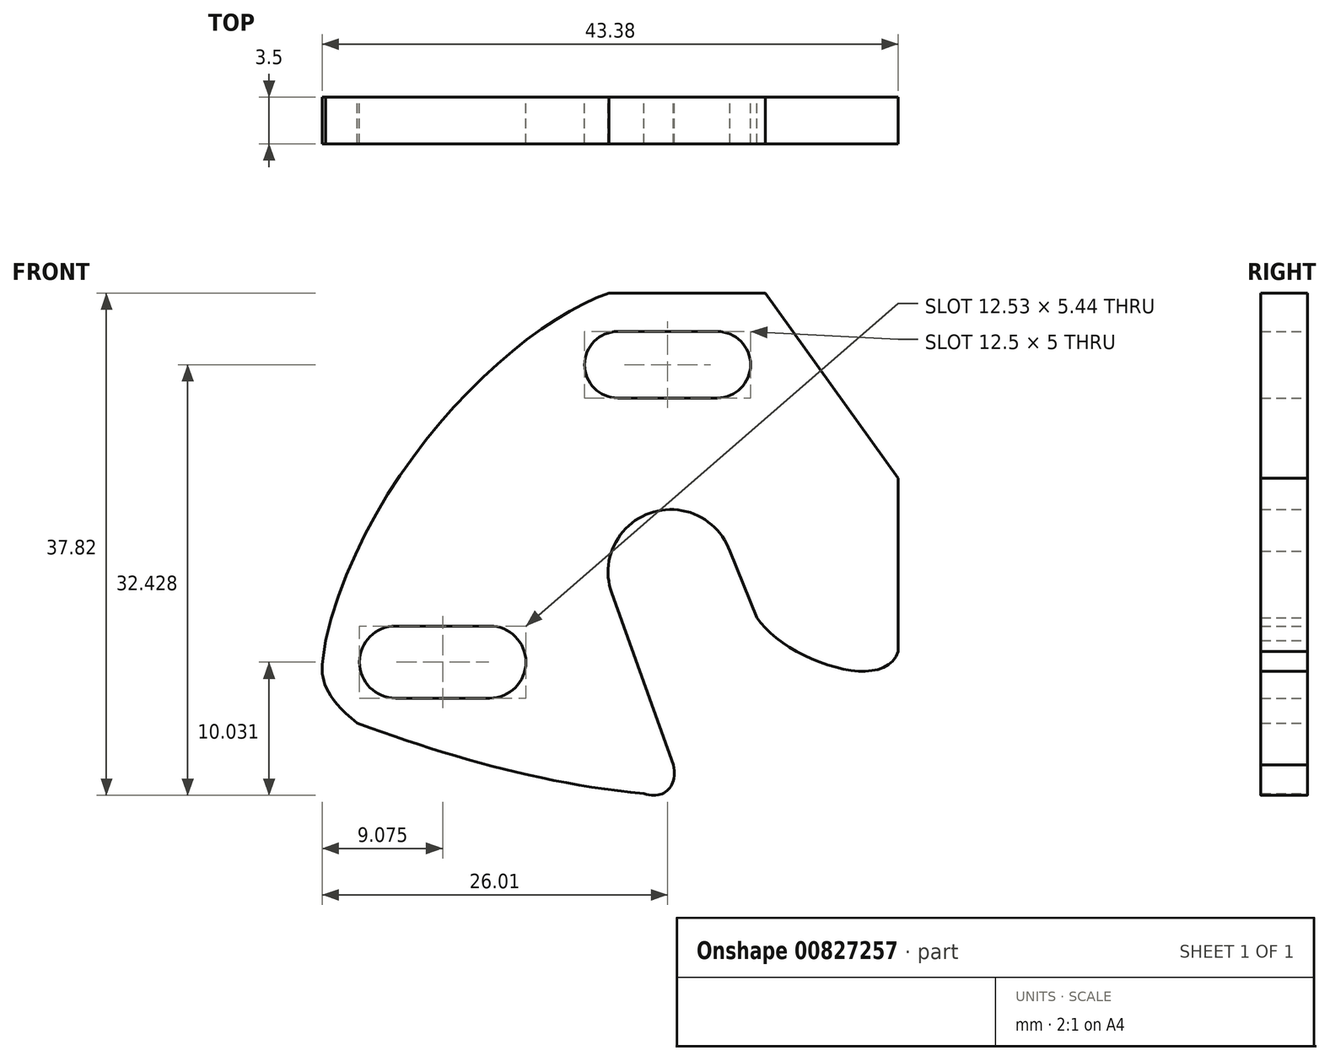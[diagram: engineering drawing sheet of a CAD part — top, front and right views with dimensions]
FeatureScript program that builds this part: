
annotation { "Feature Type Name" : "Feature", "Feature Type Description" : "" }
export const myFeature = defineFeature(function(context is Context, id is Id, definition is map)
    precondition{}
    {
        {
            var Q0;
            Q0=qCreatedBy(makeId("Front.planeOp"),FACE);
            var sketch = newSketch(context, id + "F0", { "sketchPlane" : qUnion([Q0])});
            skLineSegment(sketch, "E0", {"start": v(-0.66, 19.43) * mm, "end": v(11.11, 19.43) * mm});
            skLineSegment(sketch, "E1", {"start": v(11.11, 19.43) * mm, "end": v(21.12, 5.5) * mm});
            skLineSegment(sketch, "E2", {"start": v(21.12, 5.5) * mm, "end": v(21.12, -7.55) * mm});
            skLineSegment(sketch, "E3", {"start": v(0, 16.54) * mm, "end": v(7.5, 16.54) * mm});
            skLineSegment(sketch, "E4", {"start": v(0, 11.54) * mm, "end": v(7.5, 11.54) * mm});
            skLineSegment(sketch, "E5", {"start": v(-16.73, -5.64) * mm, "end": v(-9.64, -5.64) * mm});
            skLineSegment(sketch, "E6", {"start": v(-16.73, -11.08) * mm, "end": v(-9.64, -11.08) * mm});
            skArc(sketch, "E7", {"start": v(-9.64, -5.64) * mm, "mid": v(-6.92, -8.36) * mm, "end": v(-9.64, -11.08) * mm});
            skArc(sketch, "E8", {"start": v(-16.73, -5.64) * mm, "mid": v(-19.45, -8.36) * mm, "end": v(-16.73, -11.08) * mm});
            skArc(sketch, "E9", {"start": v(7.5, 11.54) * mm, "mid": v(10, 14.04) * mm, "end": v(7.5, 16.54) * mm});
            skArc(sketch, "E10", {"start": v(0, 16.54) * mm, "mid": v(-2.5, 14.04) * mm, "end": v(0, 11.54) * mm});
            skArc(sketch, "E11", {"start": v(8.44, 0) * mm, "mid": v(2.4, 2.86) * mm, "end": v(-0.45, -3.18) * mm});
            skLineSegment(sketch, "E12", {"start": v(8.44, 0) * mm, "end": v(10.48, -5.01) * mm});
            skLineSegment(sketch, "E13", {"start": v(-0.45, -3.18) * mm, "end": v(4.18, -16.1) * mm});
            skFitSpline(sketch, "E14", {"points": [v(21.12, -7.55) * mm, v(10.48, -5.01) * mm], "startDerivative": vector(-3.35, -9.96) * mm, "endDerivative": vector(-5.83, 9.1) * mm});
            skFitSpline(sketch, "E15", {"points": [v(-0.66, 19.43) * mm, v(-22.02, -6.74) * mm], "startDerivative": vector(-21.34, -7.25) * mm, "endDerivative": vector(-9.12, -38.56) * mm});
            skFitSpline(sketch, "E16", {"points": [v(-22.02, -6.74) * mm, v(-19.6, -12.97) * mm], "startDerivative": vector(-0.16, -5.18) * mm, "endDerivative": vector(11.15, -8.95) * mm});
            skFitSpline(sketch, "E17", {"points": [v(-19.6, -12.97) * mm, v(1.97, -18.27) * mm], "startDerivative": vector(21.32, -7.76) * mm, "endDerivative": vector(23.07, -2.3) * mm});
            skFitSpline(sketch, "E18", {"points": [v(1.97, -18.27) * mm, v(4.18, -16.1) * mm], "startDerivative": vector(4.45, -1.36) * mm, "endDerivative": vector(-1.11, 5.18) * mm});
            skSolve(sketch);
        }
        {
            var Q0;
            Q0=makeQuery(id+"F0.imprint","IMPRINT",FACE,{"disambiguationData":[TD([[makeQuery(id+"F0.imprint","IMPRINT",EDGE,{"derivedFrom":sQuery(id+"F0.wireOp",EDGE,"E0")}),-1.0]])]});
            extrude(context, id + "F1", {"entities" : qUnion([Q0]), "depth" : 3.5 * mm, "offsetDistance" : 25 * mm});
        }
    });
